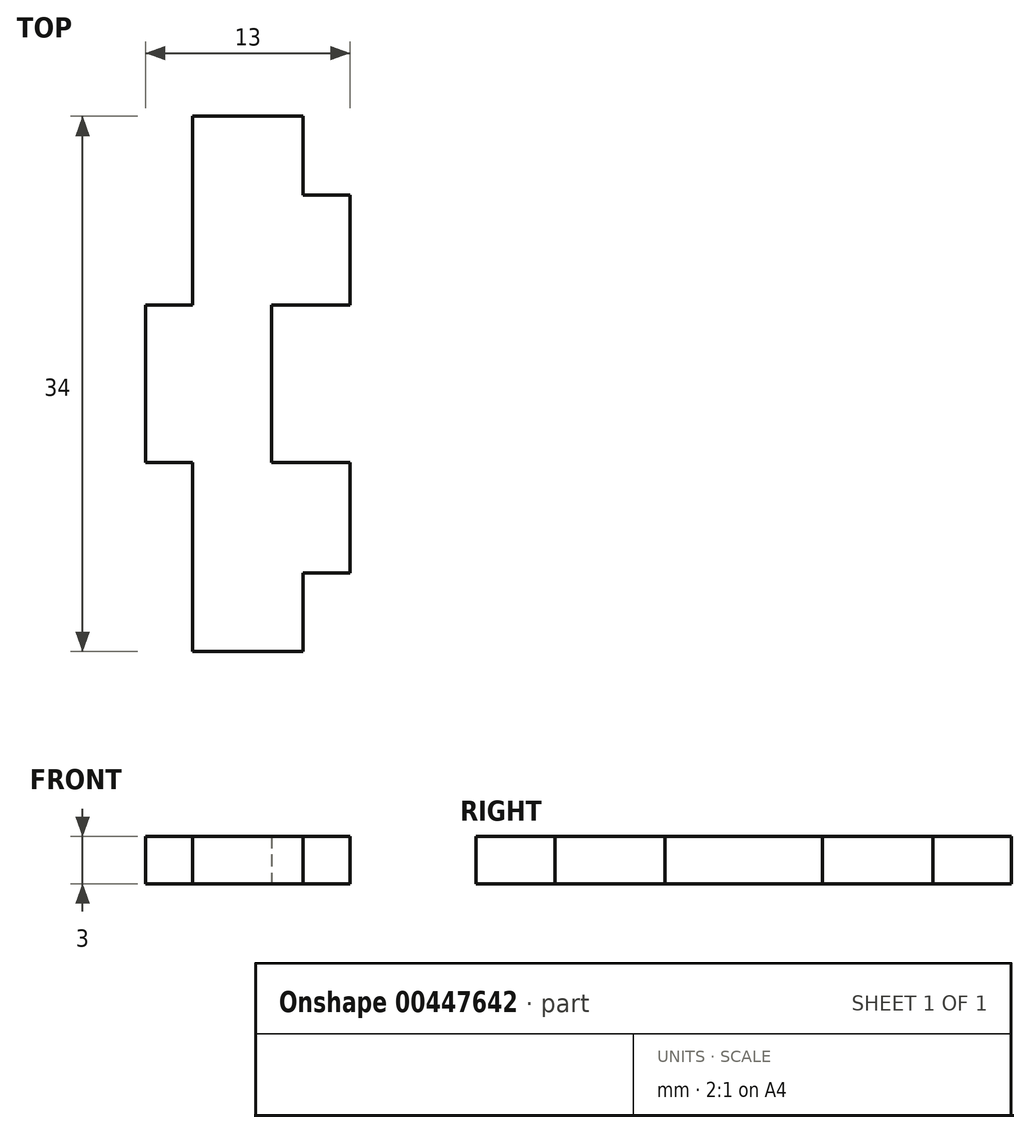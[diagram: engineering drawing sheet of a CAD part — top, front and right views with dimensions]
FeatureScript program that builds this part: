
annotation { "Feature Type Name" : "Feature", "Feature Type Description" : "" }
export const myFeature = defineFeature(function(context is Context, id is Id, definition is map)
    precondition{}
    {
        {
            var Q0;
            Q0=qCreatedBy(makeId("Top.planeOp"),FACE);
            var sketch = newSketch(context, id + "F0", { "sketchPlane" : qUnion([Q0])});
            skPoint(sketch, "E0.middle", {"position": v(0, 0) * mm});
            skLineSegment(sketch, "E1.bottom", {"start": v(-5, -5) * mm, "end": v(-8, -5) * mm});
            skLineSegment(sketch, "E1.top", {"start": v(-5, 5) * mm, "end": v(-8, 5) * mm});
            skLineSegment(sketch, "E1.right", {"start": v(-8, -5) * mm, "end": v(-8, 5) * mm});
            skPoint(sketch, "E1.middle", {"position": v(-6.5, 0) * mm});
            skLineSegment(sketch, "E2.right", {"start": v(2, -17) * mm, "end": v(2, -12) * mm});
            skLineSegment(sketch, "E3.bottom", {"start": v(5, 12) * mm, "end": v(2, 12) * mm});
            skLineSegment(sketch, "E4.right", {"start": v(0, -5) * mm, "end": v(0, 5) * mm});
            skPoint(sketch, "E4.middle", {"position": v(2.5, 0) * mm});
            skLineSegment(sketch, "E5", {"start": v(-5, 17) * mm, "end": v(2, 17) * mm});
            skLineSegment(sketch, "E6", {"start": v(5, 5) * mm, "end": v(5, 12) * mm});
            skLineSegment(sketch, "E7", {"start": v(5, -12) * mm, "end": v(2, -12) * mm});
            skLineSegment(sketch, "E8", {"start": v(2, -17) * mm, "end": v(-5, -17) * mm});
            skLineSegment(sketch, "E9", {"start": v(5, -12) * mm, "end": v(5, -5) * mm});
            skLineSegment(sketch, "E10", {"start": v(2, 12) * mm, "end": v(2, 17) * mm});
            skLineSegment(sketch, "E11", {"start": v(0, 5) * mm, "end": v(5, 5) * mm});
            skLineSegment(sketch, "E12", {"start": v(0, -5) * mm, "end": v(5, -5) * mm});
            skLineSegment(sketch, "E13", {"start": v(-5, 5) * mm, "end": v(-5, 17) * mm});
            skLineSegment(sketch, "E14", {"start": v(-5, -5) * mm, "end": v(-5, -17) * mm});
            skSolve(sketch);
        }
        {
            var Q0;
            Q0=makeQuery(id+"F0.imprint","IMPRINT",FACE,{"disambiguationData":[TD([[makeQuery(id+"F0.imprint","IMPRINT",EDGE,{"derivedFrom":sQuery(id+"F0.wireOp",EDGE,"E1.bottom")}),-1.0]])]});
            var Q1;
            {var subQ1=sQuery(id+"F0.wireOp",EDGE,"E0.bottom");Q1=makeQuery(id+"F0.imprint","IMPRINT",FACE,{"disambiguationData":[TD([[makeQuery(id+"F0.imprint","IMPRINT",EDGE,{"derivedFrom":subQ1}),-1.0]])]});}
            extrude(context, id + "F1", {"entities" : qUnion([Q0, Q1]), "depth" : 3 * mm});
        }
    });
